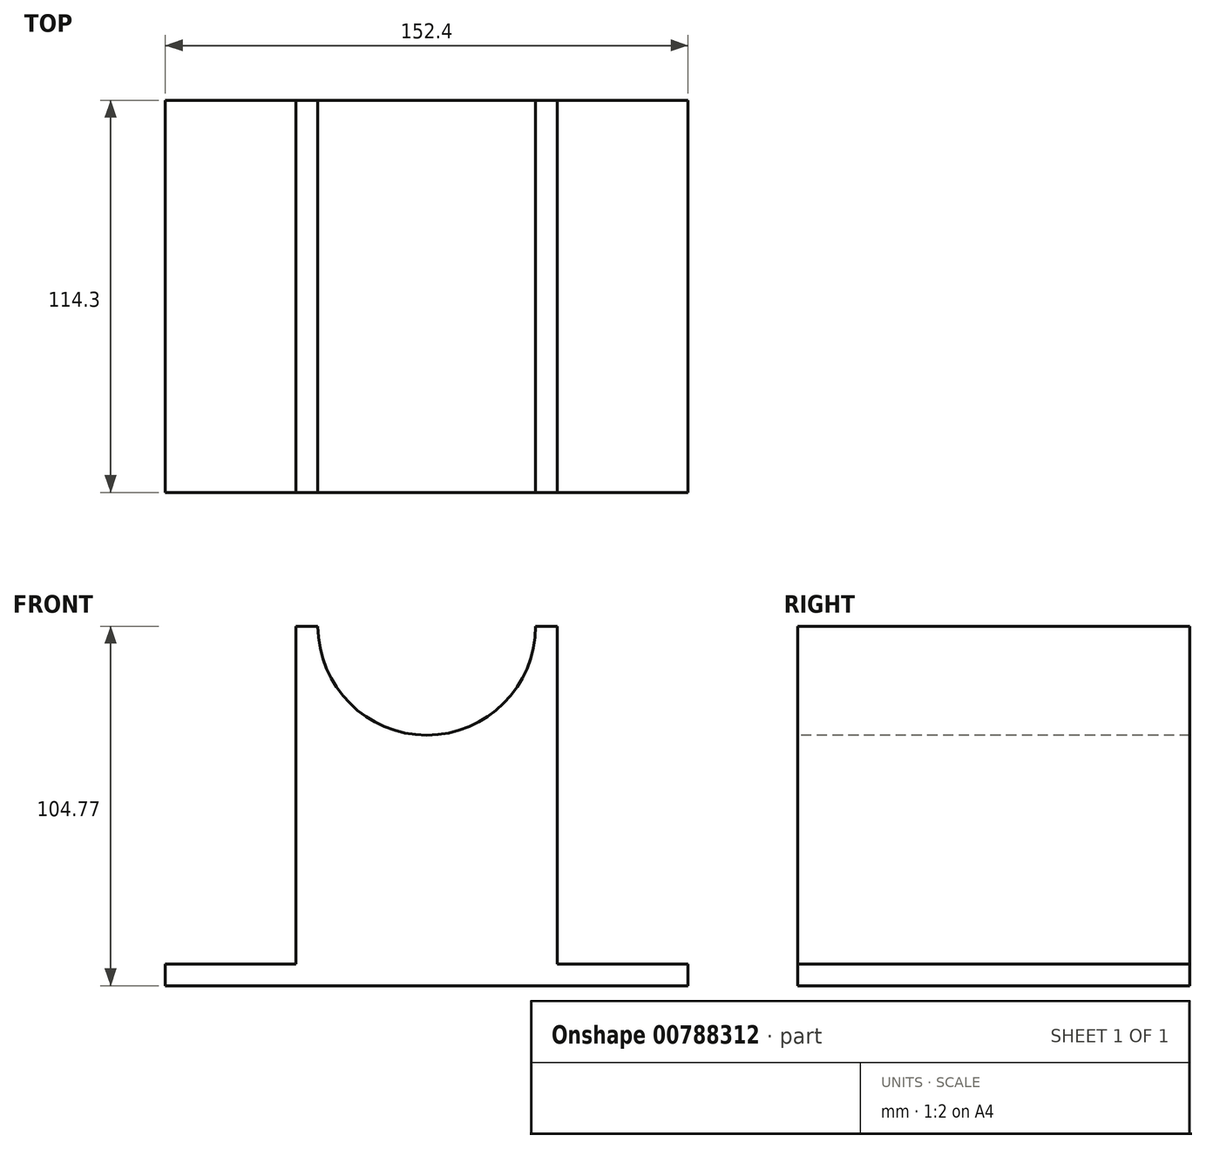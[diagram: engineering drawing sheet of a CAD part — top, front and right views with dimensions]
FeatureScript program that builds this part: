
annotation { "Feature Type Name" : "Feature", "Feature Type Description" : "" }
export const myFeature = defineFeature(function(context is Context, id is Id, definition is map)
    precondition{}
    {
        {
            var Q0;
            Q0=qCreatedBy(makeId("Front.planeOp"),FACE);
            var sketch = newSketch(context, id + "F0", { "sketchPlane" : qUnion([Q0])});
            skLineSegment(sketch, "E0", {"start": v(2.64, 0) * mm, "end": v(155.04, 0) * mm});
            skLineSegment(sketch, "E1", {"start": v(2.64, 0) * mm, "end": v(2.64, 6.35) * mm});
            skLineSegment(sketch, "E2", {"start": v(155.04, 0) * mm, "end": v(155.04, 6.35) * mm});
            skLineSegment(sketch, "E3", {"start": v(2.64, 6.35) * mm, "end": v(40.74, 6.35) * mm});
            skLineSegment(sketch, "E4", {"start": v(155.04, 6.35) * mm, "end": v(116.94, 6.35) * mm});
            skLineSegment(sketch, "E5", {"start": v(40.74, 6.35) * mm, "end": v(40.74, 104.78) * mm});
            skLineSegment(sketch, "E6", {"start": v(116.94, 6.35) * mm, "end": v(116.94, 104.78) * mm});
            skLineSegment(sketch, "E7", {"start": v(116.94, 104.78) * mm, "end": v(40.74, 104.78) * mm});
            skSolve(sketch);
        }
        {
            var Q0;
            Q0=makeQuery(id+"F0.imprint","IMPRINT",FACE,{"disambiguationData":[TD([[makeQuery(id+"F0.imprint","IMPRINT",EDGE,{"derivedFrom":sQuery(id+"F0.wireOp",EDGE,"E0")}),1.0]])]});
            extrude(context, id + "F1", {"entities" : qUnion([Q0]), "depth" : 114.3 * mm, "offsetDistance" : 25.4 * mm});
        }
        {
            var Q0;
            Q0=makeQuery(id+"F1.opExtrude","CAP_FACE",FACE,{"disambiguationData":[OSD([sQuery(id+"F0.wireOp",EDGE,"E0"),sQuery(id+"F0.wireOp",EDGE,"E1"),sQuery(id+"F0.wireOp",EDGE,"E2"),sQuery(id+"F0.wireOp",EDGE,"E3"),sQuery(id+"F0.wireOp",EDGE,"E4"),sQuery(id+"F0.wireOp",EDGE,"E5"),sQuery(id+"F0.wireOp",EDGE,"E6"),sQuery(id+"F0.wireOp",EDGE,"E7")])],"isStart":false});
            var sketch = newSketch(context, id + "F2", { "sketchPlane" : qUnion([Q0])});
            skLineSegment(sketch, "E8", {"start": v(40.74, 104.78) * mm, "end": v(47.09, 104.78) * mm, "construction": true});
            skLineSegment(sketch, "E9", {"start": v(116.94, 104.78) * mm, "end": v(110.59, 104.78) * mm, "construction": true});
            skArc(sketch, "E10", {"start": v(47.09, 104.78) * mm, "mid": v(78.84, 73.03) * mm, "end": v(110.59, 104.78) * mm});
            skSolve(sketch);
        }
        {
            var Q0;
            {var subQ0=sQuery(id+"F2.wireOp",EDGE,"E10");Q0=makeQuery(id+"F2.imprint","IMPRINT",FACE,{"disambiguationData":[TD([[makeQuery(id+"F2.imprint","IMPRINT",EDGE,{"derivedFrom":subQ0}),1.0]])]});}
            extrude(context, id + "F3", {"entities" : qUnion([Q0]), "operationType" : NewBodyOperationType.REMOVE, "endBound" : BoundingType.UP_TO_NEXT, "oppositeDirection" : true, "depth" : 25.4 * mm, "offsetDistance" : 25.4 * mm});
        }
    });
